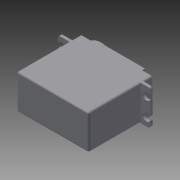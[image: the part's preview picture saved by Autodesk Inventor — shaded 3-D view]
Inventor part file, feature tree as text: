
AUTODESK INVENTOR PART (.ipt)
format: ipt  version: 2015 SP2 (Build 190223200, 223)  size: 212,480 bytes
history: native  units: mm
features: sketch x17, extrude x9, fillet x5, hole x1, plane x1, mirror x1
ambient origin geometry x8: Origin, YZ Plane, XZ Plane, XY Plane, X Axis, Y Axis, Z Axis, Center Point
bodies: Body1 (feature_tree)
feature tree (34):
  extrude  "Extrusion2"  Depth=40.3mm
  sketch  "Sketch5"  dims[d8=35.5mm d9=0.0mm d10=2.0mm d11=0.0mm]
  sketch  "Sketch6"  dims[d12=2.0mm d13=0.0mm d14=1.8mm d15=0.0mm]
  sketch  "Sketch7"  dims[d16=12.79mm d17=1.2mm d18=0.0mm]
  extrude  "Extrusion3"  Depth=2.0mm TaperAngle=0.0deg
  extrude  "Extrusion4"  Depth=1.8mm TaperAngle=0.0deg
  extrude  "Extrusion5"  Depth=1.2mm TaperAngle=0.0deg
  extrude  "Extrusion6"  Depth=0.6mm
  extrude  "Extrusion7"  Depth=3.0mm TaperAngle=0.0deg
  extrude  "Extrusion8"  Depth=5.8mm TaperAngle=0.0deg
  extrude  "Extrusion9"  Depth=1.0mm
  extrude  "Extrusion10"  Depth=1.0mm
  sketch  "Sketch20"
  hole  "Hole1"  [1 undecoded]
  fillet  "Fillet1"  Radius=1.0mm
  fillet  "Fillet2"  [1 undecoded]
  fillet  "Fillet3"  [1 undecoded]
  fillet  "Fillet4"  [1 undecoded]
  sketch  "Sketch24"
  plane  "Work Plane4"
  mirror  "Mirror2"
  fillet  "Fillet5"  [1 undecoded]
  sketch  "Sketch25"
  sketch  "Sketch26"
  sketch  "Sketch4"  dims[d6=19.5mm d7=40.3mm]
  sketch  "Sketch9"  dims[d19=0.6mm d20=0.0mm d21=5.7mm]
  sketch  "Sketch12"  dims[d22=3.0mm d23=0.0mm d24=3.0mm d25=0.0mm]
  sketch  "Sketch13"  dims[d26=5.0mm d27=5.8mm d28=0.0mm]
  sketch  "Sketch14"  dims[d29=4.5mm]
  sketch  "Sketch16"  dims[d30=4.5mm d31=6.0mm d32=4.0mm d33=2.0mm d34=90.0deg d35=8.0mm d36=20.594885mm d37=1.0mm]
  sketch  "Sketch17"  dims[d38=1.0mm d39=1.0mm]
  sketch  "Sketch18"  dims[d40=1.0mm d43=-1.75mm d44=1.0mm]
  sketch  "Sketch19"
  sketch  "Sketch22"
note: 5 required parameter values undecoded (feature->parameter linkage not recoverable at this tier; creation-order binding heuristic only, values carry confidence <= 0.55)
